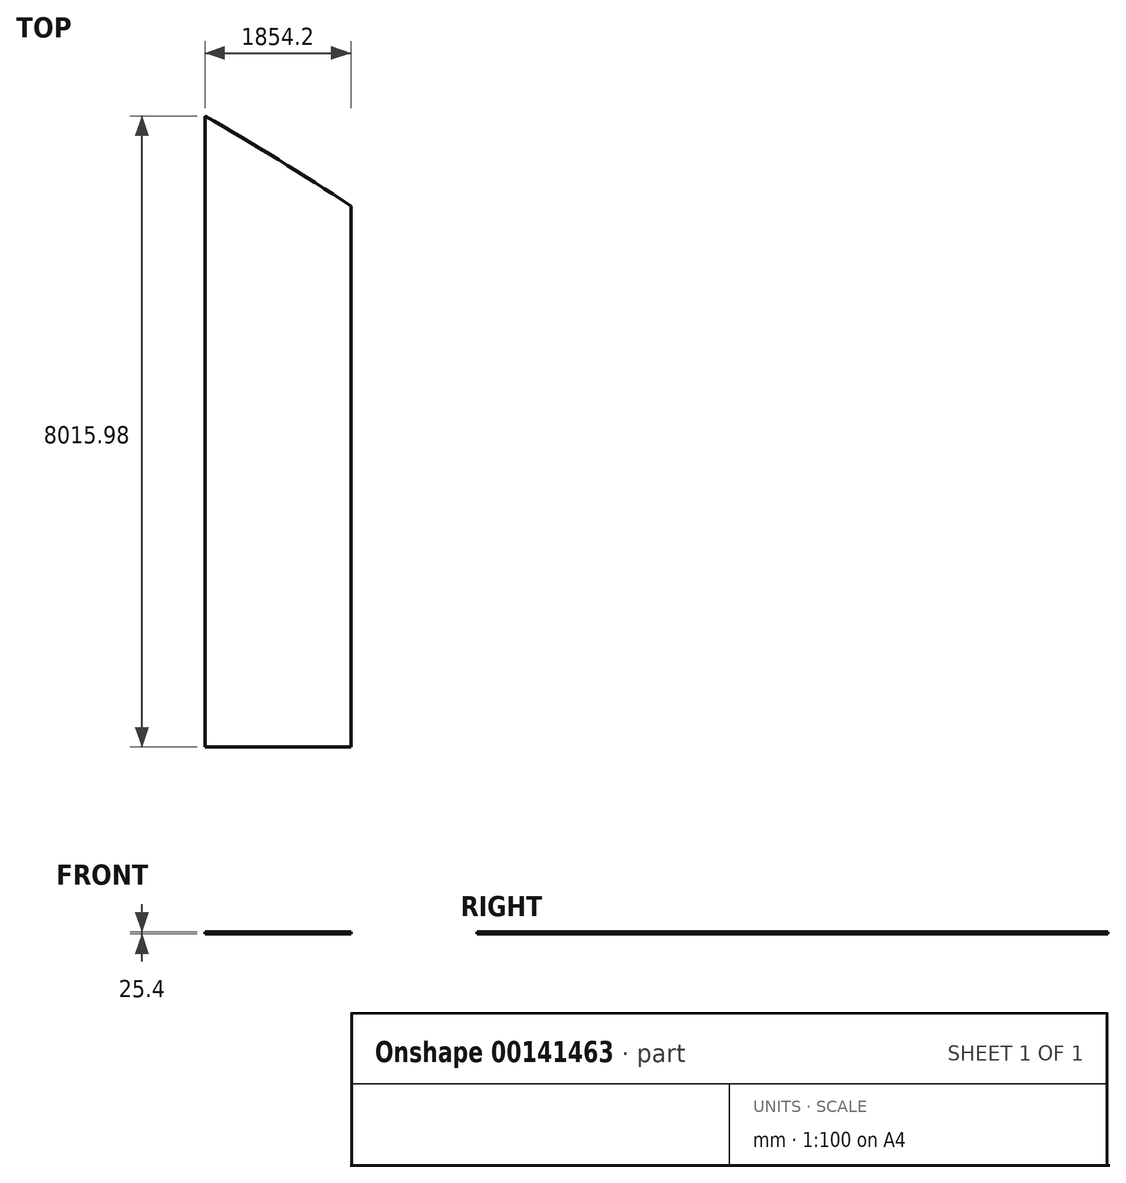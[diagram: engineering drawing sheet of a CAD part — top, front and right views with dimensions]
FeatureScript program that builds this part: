
annotation { "Feature Type Name" : "Feature", "Feature Type Description" : "" }
export const myFeature = defineFeature(function(context is Context, id is Id, definition is map)
    precondition{}
    {
        {
            var Q0;
            Q0=qCreatedBy(makeId("Top.planeOp"),FACE);
            var sketch = newSketch(context, id + "F0", { "sketchPlane" : qUnion([Q0])});
            skLineSegment(sketch, "E0", {"start": v(-957.26, -3909.03) * mm, "end": v(896.94, -3909.03) * mm});
            skLineSegment(sketch, "E1", {"start": v(-957.26, -3909.03) * mm, "end": v(-957.26, 4106.95) * mm});
            skLineSegment(sketch, "E2", {"start": v(896.94, -3909.03) * mm, "end": v(896.94, 2961.67) * mm});
            skLineSegment(sketch, "E3", {"start": v(-30.16, -3909.03) * mm, "end": v(-30.16, 3556.28) * mm});
            skArc(sketch, "E4", {"start": v(896.94, 2961.67) * mm, "mid": v(-20.34, 3550.21) * mm, "end": v(-957.26, 4106.95) * mm});
            skSolve(sketch);
        }
        {
            var Q0;
            {var subQ0=sQuery(id+"F0.wireOp",EDGE,"E1");Q0=makeQuery(id+"F0.imprint","IMPRINT",FACE,{"disambiguationData":[TD([[makeQuery(id+"F0.imprint","IMPRINT",EDGE,{"derivedFrom":subQ0}),-1.0]])]});}
            var Q1;
            {var subQ0=sQuery(id+"F0.wireOp",EDGE,"E2");Q1=makeQuery(id+"F0.imprint","IMPRINT",FACE,{"disambiguationData":[TD([[makeQuery(id+"F0.imprint","IMPRINT",EDGE,{"derivedFrom":subQ0}),1.0]])]});}
            extrude(context, id + "F1", {"entities" : qUnion([Q0, Q1]), "depth" : 25.4 * mm});
        }
    });
